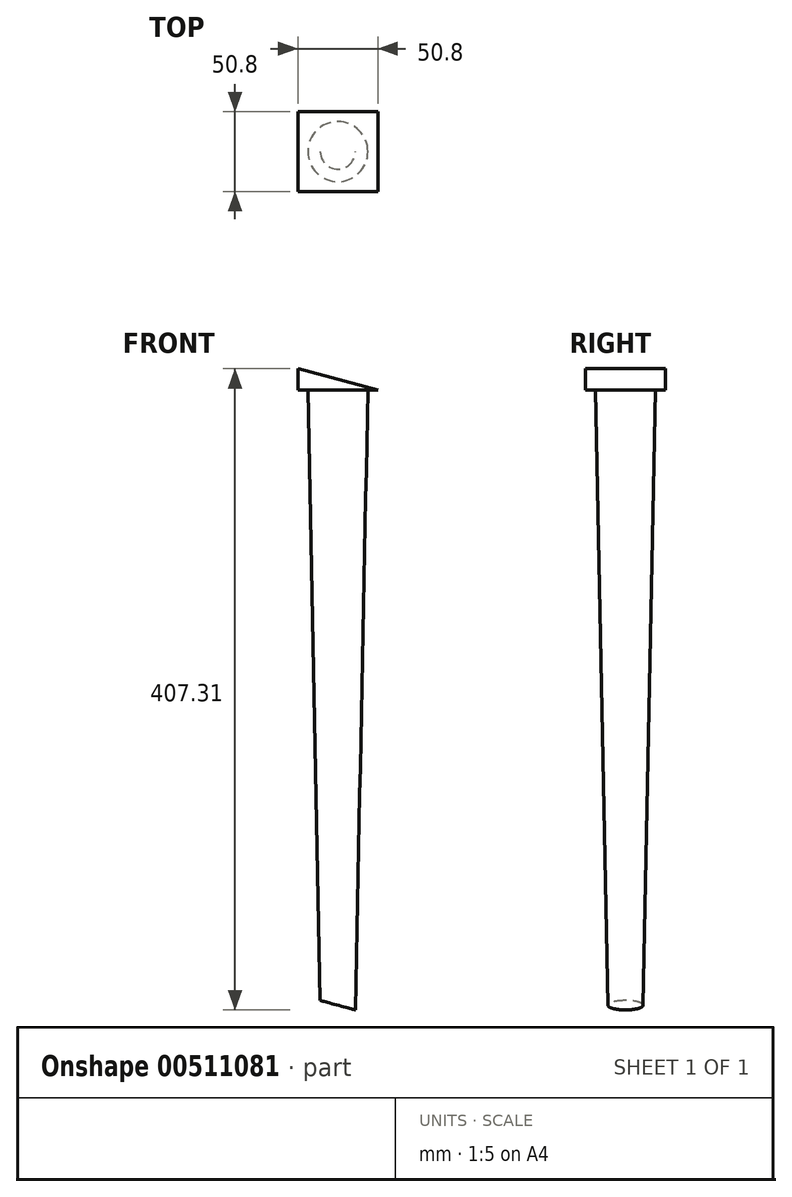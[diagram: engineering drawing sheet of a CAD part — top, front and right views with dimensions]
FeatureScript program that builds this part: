
annotation { "Feature Type Name" : "Feature", "Feature Type Description" : "" }
export const myFeature = defineFeature(function(context is Context, id is Id, definition is map)
    precondition{}
    {
        {
            var Q0;
            Q0=qCreatedBy(makeId("Top.planeOp"),FACE);
            var sketch = newSketch(context, id + "F0", { "sketchPlane" : qUnion([Q0])});
            skCircle(sketch, "E0", {"center": v(0, 0) * mm, "radius": 19.05 * mm});
            skSolve(sketch);
        }
        {
            var Q0;
            Q0=qCreatedBy(makeId("Top.planeOp"),FACE);
            cPlane(context, id + "F1", {"entities" : qUnion([Q0]), "cplaneType" : CPlaneType.OFFSET, "offset" : 393.7 * mm, "oppositeDirection" : true, "width" : 152.4 * mm, "height" : 152.4 * mm});
        }
        {
            var Q0;
            Q0=qCreatedBy(id+"F1.planeOp",FACE);
            var sketch = newSketch(context, id + "F2", { "sketchPlane" : qUnion([Q0])});
            skCircle(sketch, "E1", {"center": v(0, 0) * mm, "radius": 11.11 * mm});
            skSolve(sketch);
        }
        {
            var Q0;
            Q0=makeQuery(id+"F0.imprint","IMPRINT",FACE,{"disambiguationData":[TD([[makeQuery(id+"F0.imprint","IMPRINT",EDGE,{"derivedFrom":sQuery(id+"F0.wireOp",EDGE,"E0")}),1.0]])]});
            var Q1;
            Q1=makeQuery(id+"F2.imprint","IMPRINT",FACE,{"disambiguationData":[TD([[makeQuery(id+"F2.imprint","IMPRINT",EDGE,{"derivedFrom":sQuery(id+"F2.wireOp",EDGE,"E1")}),1.0]])]});
            loft(context, id + "F3", {"sheetProfilesArray" : [{ "sheetProfileEntities" : qUnion([Q0]) }, { "sheetProfileEntities" : qUnion([Q1]) }]});
        }
        {
            var Q0;
            Q0=qCreatedBy(makeId("Front.planeOp"),FACE);
            var sketch = newSketch(context, id + "F4", { "sketchPlane" : qUnion([Q0])});
            skLineSegment(sketch, "E2", {"start": v(25.4, 0) * mm, "end": v(-25.4, 0) * mm});
            skLineSegment(sketch, "E3", {"start": v(-25.4, 0) * mm, "end": v(-25.4, 13.61) * mm});
            skLineSegment(sketch, "E4", {"start": v(-25.4, 13.61) * mm, "end": v(25.4, 0) * mm});
            skSolve(sketch);
        }
        {
            var Q0;
            Q0=makeQuery(id+"F4.imprint","IMPRINT",FACE,{"disambiguationData":[TD([[makeQuery(id+"F4.imprint","IMPRINT",EDGE,{"derivedFrom":sQuery(id+"F4.wireOp",EDGE,"E2")}),-1.0]])]});
            extrude(context, id + "F5", {"entities" : qUnion([Q0]), "depth" : 50.8 * mm, "offsetDistance" : 25.4 * mm, "symmetric" : true});
        }
        {
            var Q0;
            Q0=qCreatedBy(makeId("Front.planeOp"),FACE);
            var sketch = newSketch(context, id + "F6", { "sketchPlane" : qUnion([Q0])});
            skLineSegment(sketch, "E5", {"start": v(-14.29, -393.7) * mm, "end": v(11.11, -393.7) * mm});
            skLineSegment(sketch, "E6", {"start": v(11.11, -393.7) * mm, "end": v(-14.29, -386.9) * mm});
            skLineSegment(sketch, "E7", {"start": v(-14.29, -386.9) * mm, "end": v(-14.29, -393.7) * mm});
            skLineSegment(sketch, "E8.0", {"start": v(11.11, -393.7) * mm, "end": v(-14.29, -393.7) * mm});
            skSolve(sketch);
        }
        {
            var Q0;
            Q0 = qSketchRegion(id + "F6", true);
            extrude(context, id + "F7", {"entities" : qUnion([Q0]), "operationType" : NewBodyOperationType.REMOVE, "oppositeDirection" : true, "depth" : 25.4 * mm, "offsetDistance" : 25.4 * mm, "symmetric" : true});
        }
    });
